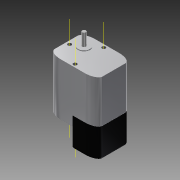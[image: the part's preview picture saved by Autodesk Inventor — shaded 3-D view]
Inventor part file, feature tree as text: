
AUTODESK INVENTOR PART (.ipt)
format: ipt  version: 2013 (Build 170138000, 138)  size: 232,448 bytes
history: native  units: mm
features: extrude x6, sketch x6, thread x3, other x3, fillet x2
ambient origin geometry x8: Origin, YZ Plane, XZ Plane, XY Plane, X Axis, Y Axis, Z Axis, Center Point
feature tree (20):
  extrude  "Extrusion2"  Depth=29.0mm
  extrude  "Extrusion3"  Depth=3.0mm
  thread  "Thread1"  [1 undecoded]
  thread  "Thread2"  [1 undecoded]
  thread  "Thread3"  [1 undecoded]
  extrude  "Extrusion4"  Depth=5.0mm TaperAngle=0.0deg
  extrude  "Extrusion5"  Depth=10.0mm TaperAngle=0.0deg
  extrude  "Extrusion6"  Depth=11.5mm
  sketch  "Sketch6"  dims[d33=3.0mm d34=1.5mm d35=1.5mm d36=11.0mm d37=0.0mm d38=0.67mm d39=0.0mm d40=10.0mm d42=40.0mm d43=20.0mm d44=8.0mm d45=0.0mm d49=0.5mm d50=24.0mm d51=0.0mm d52=2.0mm]
  fillet  "Fillet2"  Radius=12.0mm
  extrude  "Extrusion8"  Depth=1.5mm
  fillet  "Fillet3"  Radius=1.5mm
  other  "Work Axis1"
  other  "Work Axis2"
  other  "Work Axis3"
  sketch  "Sketch1"  dims[d12=36.0mm d13=0.0mm d16=29.0mm]
  sketch  "Sketch2"  dims[d17=14.5mm d18=3.0mm d19=3.0mm d20=24.0mm d21=12.0mm]
  sketch  "Sketch3"  dims[d22=16.5mm d23=5.0mm d24=0.0mm]
  sketch  "Sketch4"  dims[d25=10.0mm d26=0.0mm d27=10.0mm d28=0.0mm]
  sketch  "Sketch5"  dims[d29=10.0mm d30=0.0mm d31=11.5mm d32=12.0mm]
note: 3 required parameter values undecoded (feature->parameter linkage not recoverable at this tier; creation-order binding heuristic only, values carry confidence <= 0.55)
